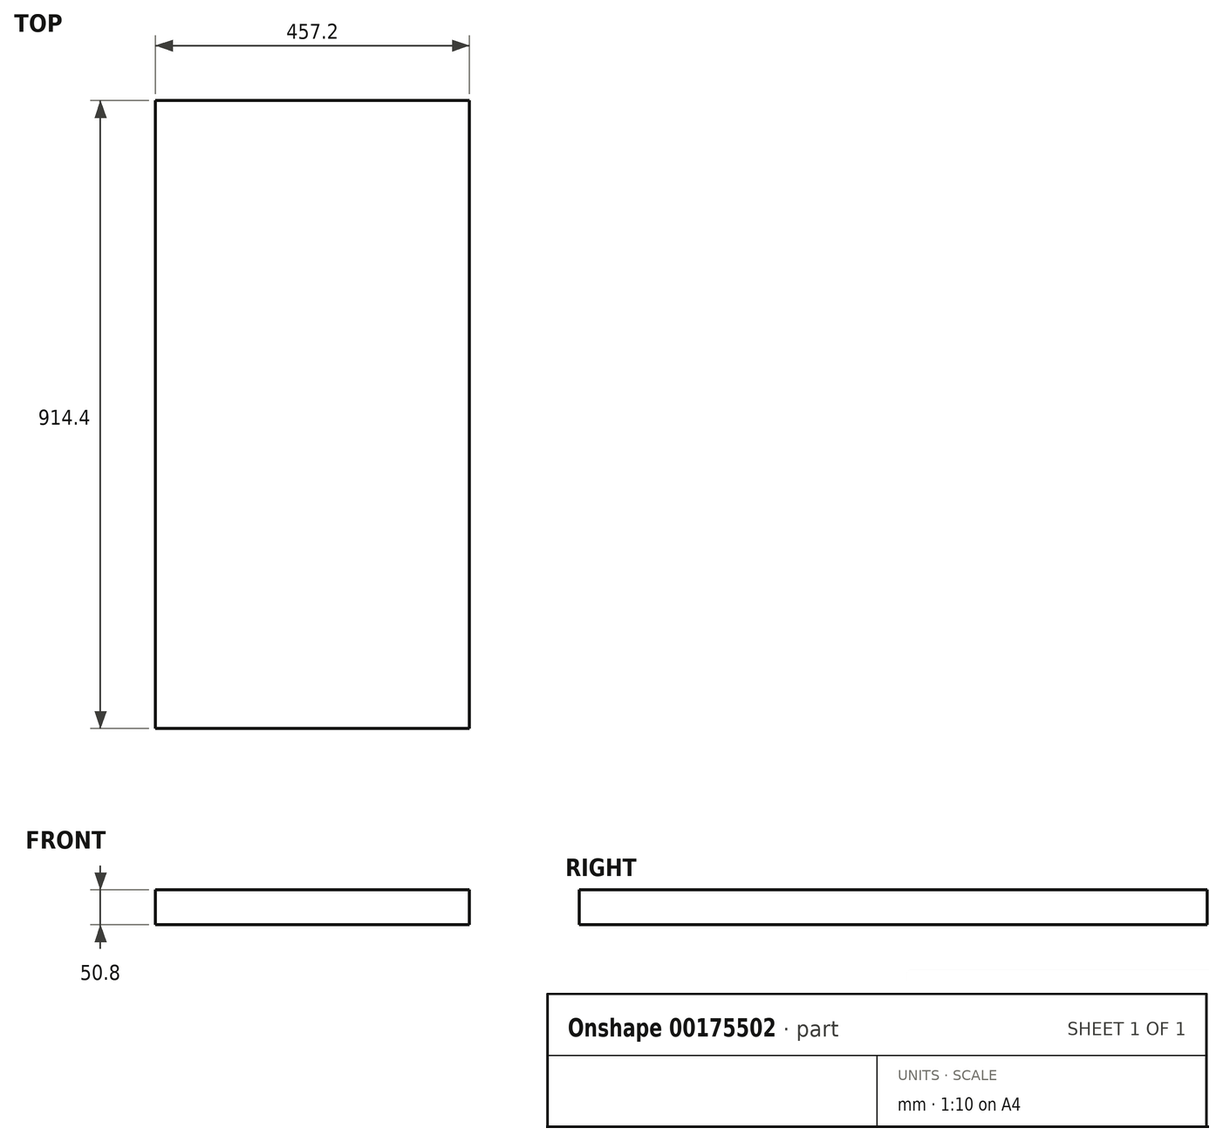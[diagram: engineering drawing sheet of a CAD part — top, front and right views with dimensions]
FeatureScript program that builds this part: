
annotation { "Feature Type Name" : "Feature", "Feature Type Description" : "" }
export const myFeature = defineFeature(function(context is Context, id is Id, definition is map)
    precondition{}
    {
        {
            var Q0;
            Q0=qCreatedBy(makeId("Top.planeOp"),FACE);
            var sketch = newSketch(context, id + "F0", { "sketchPlane" : qUnion([Q0])});
            skLineSegment(sketch, "E0.bottom", {"start": v(-228.6, 457.2) * mm, "end": v(228.6, 457.2) * mm});
            skLineSegment(sketch, "E0.top", {"start": v(-228.6, -457.2) * mm, "end": v(228.6, -457.2) * mm});
            skLineSegment(sketch, "E0.left", {"start": v(-228.6, 457.2) * mm, "end": v(-228.6, -457.2) * mm});
            skLineSegment(sketch, "E0.right", {"start": v(228.6, 457.2) * mm, "end": v(228.6, -457.2) * mm});
            skPoint(sketch, "E0.middle", {"position": v(0, 0) * mm});
            skSolve(sketch);
        }
        {
            var Q0;
            Q0 = qSketchRegion(id + "F0", true);
            extrude(context, id + "F1", {"entities" : qUnion([Q0]), "depth" : 50.8 * mm});
        }
    });
